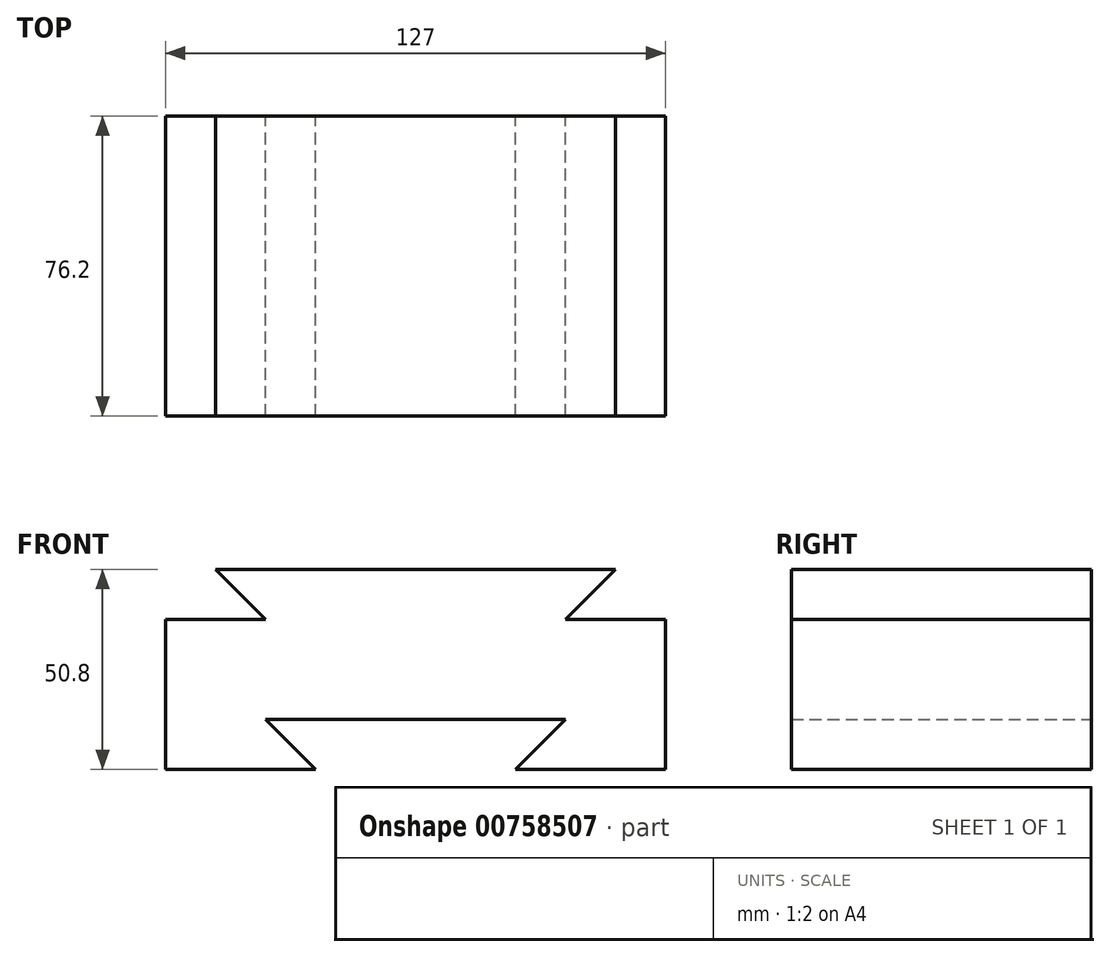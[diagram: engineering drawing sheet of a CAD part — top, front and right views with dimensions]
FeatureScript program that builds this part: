
annotation { "Feature Type Name" : "Feature", "Feature Type Description" : "" }
export const myFeature = defineFeature(function(context is Context, id is Id, definition is map)
    precondition{}
    {
        {
            var Q0;
            Q0=qCreatedBy(makeId("Front.planeOp"),FACE);
            var sketch = newSketch(context, id + "F0", { "sketchPlane" : qUnion([Q0])});
            skLineSegment(sketch, "E0", {"start": v(-151.35, 57.85) * mm, "end": v(-49.75, 57.85) * mm});
            skLineSegment(sketch, "E1", {"start": v(-151.35, 57.85) * mm, "end": v(-138.65, 45.15) * mm});
            skLineSegment(sketch, "E2", {"start": v(-49.75, 57.85) * mm, "end": v(-62.45, 45.15) * mm});
            skLineSegment(sketch, "E3", {"start": v(-62.45, 45.15) * mm, "end": v(-37.05, 45.15) * mm});
            skLineSegment(sketch, "E4", {"start": v(-164.05, 45.15) * mm, "end": v(-138.65, 45.15) * mm});
            skLineSegment(sketch, "E5", {"start": v(-37.05, 45.15) * mm, "end": v(-37.05, 7.05) * mm});
            skLineSegment(sketch, "E6", {"start": v(-164.05, 45.15) * mm, "end": v(-164.05, 7.05) * mm});
            skLineSegment(sketch, "E7", {"start": v(-164.05, 7.05) * mm, "end": v(-125.95, 7.05) * mm});
            skLineSegment(sketch, "E8", {"start": v(-75.15, 7.05) * mm, "end": v(-37.05, 7.05) * mm});
            skLineSegment(sketch, "E9", {"start": v(-138.65, 19.75) * mm, "end": v(-125.95, 7.05) * mm});
            skLineSegment(sketch, "E10", {"start": v(-62.45, 19.75) * mm, "end": v(-75.15, 7.05) * mm});
            skLineSegment(sketch, "E11", {"start": v(-138.65, 19.75) * mm, "end": v(-62.45, 19.75) * mm});
            skSolve(sketch);
        }
        {
            var Q0;
            Q0=makeQuery(id+"F0.imprint","IMPRINT",FACE,{"disambiguationData":[TD([[makeQuery(id+"F0.imprint","IMPRINT",EDGE,{"derivedFrom":sQuery(id+"F0.wireOp",EDGE,"E0")}),-1.0]])]});
            extrude(context, id + "F1", {"entities" : qUnion([Q0]), "depth" : 76.2 * mm, "offsetDistance" : 25.4 * mm});
        }
    });
